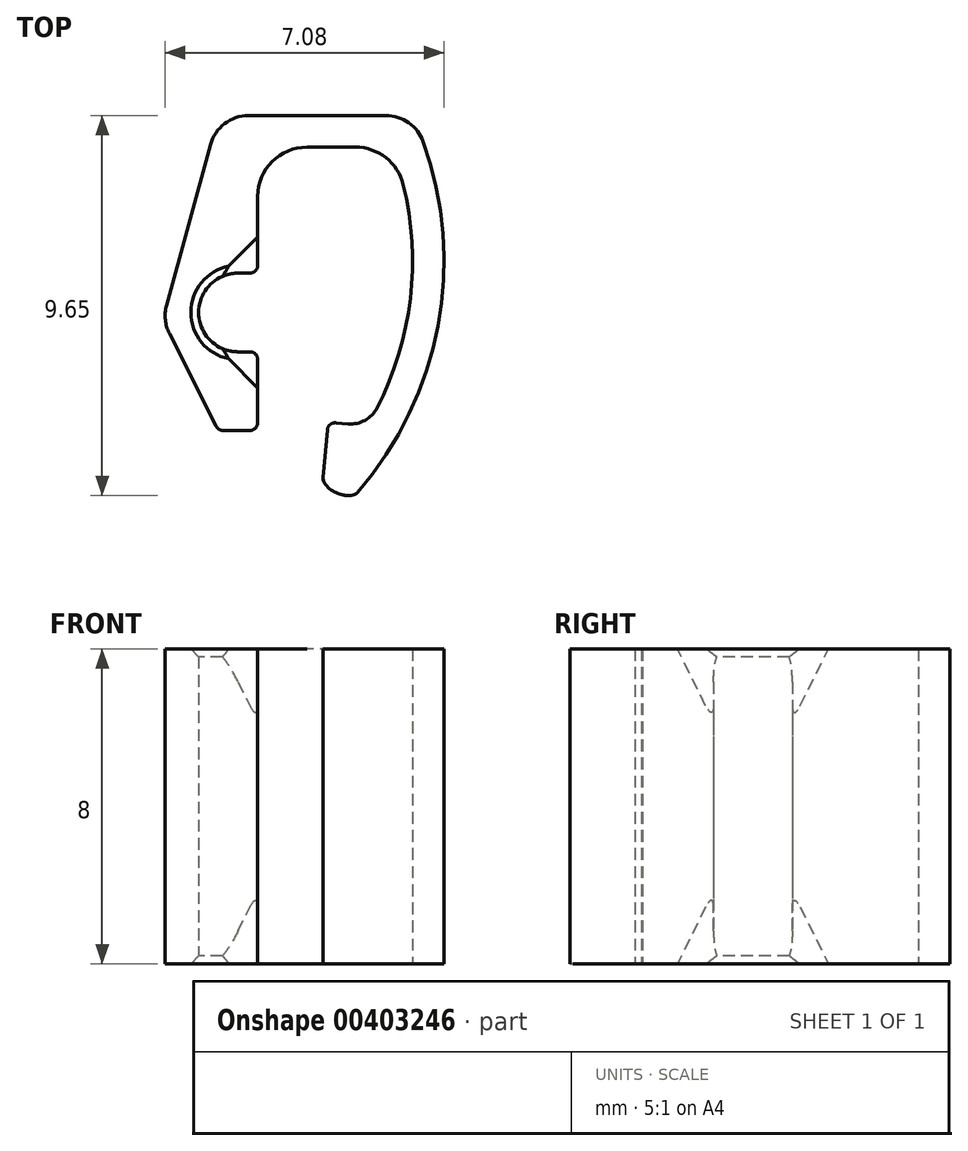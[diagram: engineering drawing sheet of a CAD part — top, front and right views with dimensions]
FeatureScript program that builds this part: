
annotation { "Feature Type Name" : "Feature", "Feature Type Description" : "" }
export const myFeature = defineFeature(function(context is Context, id is Id, definition is map)
    precondition{}
    {
        {
            var Q0;
            Q0=qCreatedBy(makeId("Top.planeOp"),FACE);
            var sketch = newSketch(context, id + "F0", { "sketchPlane" : qUnion([Q0])});
            skLineSegment(sketch, "E0", {"start": v(0, 0) * mm, "end": v(-0.62, -7.07) * mm, "construction": true});
            skLineSegment(sketch, "E1", {"start": v(-0.62, -7.07) * mm, "end": v(-1.62, -6.99) * mm});
            skLineSegment(sketch, "E2", {"start": v(-1.62, -6.99) * mm, "end": v(-1.86, -9.75) * mm});
            skLineSegment(sketch, "E3", {"start": v(0.53, 0.8) * mm, "end": v(-4.4, 0.8) * mm});
            skLineSegment(sketch, "E4", {"start": v(-3.9, -5.2) * mm, "end": v(-3.4, -5.2) * mm});
            skLineSegment(sketch, "E5", {"start": v(-3.4, -5.2) * mm, "end": v(-3.4, -7.2) * mm});
            skLineSegment(sketch, "E6", {"start": v(-5.82, -4.4) * mm, "end": v(-4.4, -7.2) * mm});
            skLineSegment(sketch, "E7", {"start": v(-4.4, -7.2) * mm, "end": v(-3.4, -7.2) * mm});
            skLineSegment(sketch, "E8", {"start": v(-3.4, -3.2) * mm, "end": v(-3.9, -3.2) * mm});
            skLineSegment(sketch, "E9", {"start": v(0, 0) * mm, "end": v(-3.4, 0) * mm});
            skLineSegment(sketch, "E10", {"start": v(-3.4, 0) * mm, "end": v(-3.4, -3.2) * mm});
            skArc(sketch, "E11", {"start": v(-3.9, -3.2) * mm, "mid": v(-4.9, -4.2) * mm, "end": v(-3.9, -5.2) * mm});
            skLineSegment(sketch, "E12", {"start": v(-5.82, -4.4) * mm, "end": v(-4.4, 0.8) * mm});
            skLineSegment(sketch, "E13", {"start": v(-4.4, -7.2) * mm, "end": v(-4.4, 0.8) * mm, "construction": true});
            skLineSegment(sketch, "E14", {"start": v(-3.9, -4.2) * mm, "end": v(-4.86, -3.94) * mm, "construction": true});
            skLineSegment(sketch, "E15", {"start": v(-4.86, -3.94) * mm, "end": v(-5.64, -3.73) * mm, "construction": true});
            skLineSegment(sketch, "E16", {"start": v(0, 0) * mm, "end": v(0, 0.8) * mm, "construction": true});
            skArc(sketch, "E17", {"start": v(-0.62, -7.07) * mm, "mid": v(0.5, -3.6) * mm, "end": v(0, 0) * mm});
            skArc(sketch, "E18", {"start": v(-1.86, -9.75) * mm, "mid": v(1.11, -4.88) * mm, "end": v(0.53, 0.8) * mm});
            skLineSegment(sketch, "E19", {"start": v(0.18, -7.3) * mm, "end": v(0.82, 0.08) * mm, "construction": true});
            skLineSegment(sketch, "E20", {"start": v(-3.4, -3.2) * mm, "end": v(-3.4, 0.8) * mm, "construction": true});
            skLineSegment(sketch, "E21", {"start": v(-3.9, -4.2) * mm, "end": v(-4.8, -4.65) * mm, "construction": true});
            skLineSegment(sketch, "E22", {"start": v(-4.8, -4.65) * mm, "end": v(-5.5, -5.01) * mm, "construction": true});
            skSolve(sketch);
        }
        {
            var Q0;
            Q0=qSketchRegion(id+"F0",true);
            extrude(context, id + "F1", {"entities" : qUnion([Q0]), "depth" : 4 * mm});
        }
        {
            var Q0;
            Q0=makeQuery(id+"F1.opExtrude","CAP_FACE",FACE,{"disambiguationData":[OSD([sQuery(id+"F0.wireOp",EDGE,"E0"),sQuery(id+"F0.wireOp",EDGE,"E1"),sQuery(id+"F0.wireOp",EDGE,"E2"),sQuery(id+"F0.wireOp",EDGE,"IWGYEIPr-8G1p-g9Af-FLij-pJIiTZfkYKLn"),sQuery(id+"F0.wireOp",EDGE,"bWUYzUkp-14V1-8Zip-sJGO-LbJPGX7ycxcC"),sQuery(id+"F0.wireOp",EDGE,"E3"),sQuery(id+"F0.wireOp",EDGE,"3qQk4eZ2-qFBK-7vCE-47k8-9gwiF50xY8QG"),sQuery(id+"F0.wireOp",EDGE,"FwfflrWr-MbD4-lGZ7-AJjG-6BkzjliF19me"),sQuery(id+"F0.wireOp",EDGE,"E4"),sQuery(id+"F0.wireOp",EDGE,"E5"),sQuery(id+"F0.wireOp",EDGE,"dEJFUDGW-VdPt-nXIw-TINV-OlQtnsbTHH9Y"),sQuery(id+"F0.wireOp",EDGE,"E6"),sQuery(id+"F0.wireOp",EDGE,"E7")])],"isStart":false});
            var sketch = newSketch(context, id + "F2", { "sketchPlane" : qUnion([Q0])});
            skLineSegment(sketch, "E23", {"start": v(-4.6, -4.9) * mm, "end": v(-3.4, -6.11) * mm});
            skLineSegment(sketch, "E24", {"start": v(-3.4, -6.11) * mm, "end": v(-3.4, -5.2) * mm});
            skLineSegment(sketch, "E25", {"start": v(-3.4, -5.2) * mm, "end": v(-4.6, -4.9) * mm});
            skLineSegment(sketch, "E26", {"start": v(-4.6, -3.5) * mm, "end": v(-3.4, -2.29) * mm});
            skLineSegment(sketch, "E27", {"start": v(-3.4, -2.29) * mm, "end": v(-3.4, -3.2) * mm});
            skLineSegment(sketch, "E28", {"start": v(-3.4, -3.2) * mm, "end": v(-4.6, -3.5) * mm});
            skSolve(sketch);
        }
        {
            var Q0;
            Q0=qSketchRegion(id+"F2",true);
            extrude(context, id + "F3", {"entities" : qUnion([Q0]), "operationType" : NewBodyOperationType.REMOVE, "oppositeDirection" : true, "depth" : 2 * mm});
        }
        {
            var Q0;
            Q0=makeQuery(id+"F3.boolean.opBoolean","COPY",EDGE,{"derivedFrom":makeQuery(id+"F3.opExtrude","CAP_EDGE",EDGE,{"disambiguationData":[OSD([sQuery(id+"F2.wireOp",EDGE,"E23")])],"isStart":false})});
            chamfer(context, id + "F4", {"entities" : qUnion([Q0]), "chamferType" : ChamferType.TWO_OFFSETS, "width1" : .7 * mm, "oppositeDirection" : false, "width2" : 2 * mm, "tangentPropagation" : true});
        }
        {
            var Q0;
            Q0=makeQuery(id+"F3.boolean.opBoolean","COPY",EDGE,{"derivedFrom":makeQuery(id+"F3.opExtrude","CAP_EDGE",EDGE,{"disambiguationData":[OSD([sQuery(id+"F2.wireOp",EDGE,"E26")])],"isStart":false})});
            chamfer(context, id + "F5", {"entities" : qUnion([Q0]), "chamferType" : ChamferType.TWO_OFFSETS, "width1" : 2 * mm, "oppositeDirection" : false, "width2" : .7 * mm, "tangentPropagation" : true});
        }
        {
            var Q0;
            Q0=makeQuery(id+"F1.opExtrude","SWEPT_EDGE",EDGE,{"disambiguationData":[OSD([sQuery(id+"F0.wireOp",EDGE,"E1"),sQuery(id+"F0.wireOp",EDGE,"E2")])]});
            var Q1;
            Q1=makeQuery(id+"F1.opExtrude","SWEPT_EDGE",EDGE,{"disambiguationData":[OSD([sQuery(id+"F0.wireOp",EDGE,"E5"),sQuery(id+"F0.wireOp",EDGE,"E7")])]});
            var Q2;
            Q2=makeQuery(id+"F1.opExtrude","SWEPT_EDGE",EDGE,{"disambiguationData":[OSD([sQuery(id+"F0.wireOp",EDGE,"E4"),sQuery(id+"F0.wireOp",EDGE,"E5")])]});
            var Q3;
            Q3=makeQuery(id+"F1.opExtrude","SWEPT_EDGE",EDGE,{"disambiguationData":[OSD([sQuery(id+"F0.wireOp",EDGE,"E8"),sQuery(id+"F0.wireOp",EDGE,"E10")])]});
            var Q4;
            Q4=makeQuery(id+"F1.opExtrude","SWEPT_EDGE",EDGE,{"disambiguationData":[OSD([sQuery(id+"F0.wireOp",EDGE,"E6"),sQuery(id+"F0.wireOp",EDGE,"E7")])]});
            fillet(context, id + "F6", {"entities" : qUnion([Q0, Q1, Q2, Q3, Q4]), "radius" : .2 * mm, "tangentPropagation" : true, "allowEdgeOverflow" : false});
        }
        {
            var Q0;
            Q0=makeQuery(id+"F1.opExtrude","SWEPT_EDGE",EDGE,{"disambiguationData":[OSD([sQuery(id+"F0.wireOp",EDGE,"bWUYzUkp-14V1-8Zip-sJGO-LbJPGX7ycxcC"),sQuery(id+"F0.wireOp",EDGE,"E3")])]});
            var Q1;
            Q1=makeQuery(id+"F1.opExtrude","SWEPT_EDGE",EDGE,{"disambiguationData":[OSD([sQuery(id+"F0.wireOp",EDGE,"IWGYEIPr-8G1p-g9Af-FLij-pJIiTZfkYKLn"),sQuery(id+"F0.wireOp",EDGE,"bWUYzUkp-14V1-8Zip-sJGO-LbJPGX7ycxcC")])]});
            var Q2;
            Q2=makeQuery(id+"F1.opExtrude","SWEPT_EDGE",EDGE,{"disambiguationData":[OSD([sQuery(id+"F0.wireOp",EDGE,"E6"),sQuery(id+"F0.wireOp",EDGE,"E7")])]});
            var Q3;
            Q3=makeQuery(id+"F1.opExtrude","SWEPT_EDGE",EDGE,{"disambiguationData":[OSD([sQuery(id+"F0.wireOp",EDGE,"E6"),sQuery(id+"F0.wireOp",EDGE,"E12")])]});
            var Q4;
            Q4=makeQuery(id+"F1.opExtrude","SWEPT_EDGE",EDGE,{"disambiguationData":[OSD([sQuery(id+"F0.wireOp",EDGE,"E3"),sQuery(id+"F0.wireOp",EDGE,"E12")])]});
            fillet(context, id + "F7", {"entities" : qUnion([Q0, Q1, Q2, Q3, Q4]), "radius" : 1 * mm, "tangentPropagation" : true, "allowEdgeOverflow" : false});
        }
        {
            var Q0;
            Q0=makeQuery(id+"F1.opExtrude","SWEPT_EDGE",EDGE,{"disambiguationData":[OSD([sQuery(id+"F0.wireOp",EDGE,"E9"),sQuery(id+"F0.wireOp",EDGE,"E10")])]});
            var Q1;
            Q1=makeQuery(id+"F1.opExtrude","SWEPT_EDGE",EDGE,{"disambiguationData":[OSD([sQuery(id+"F0.wireOp",EDGE,"E9"),sQuery(id+"F0.wireOp",EDGE,"E17")])]});
            fillet(context, id + "F8", {"entities" : qUnion([Q0, Q1]), "radius" : 1.25 * mm, "tangentPropagation" : true, "allowEdgeOverflow" : false});
        }
        {
            var Q0;
            Q0=makeQuery(id+"F1.opExtrude","CAP_EDGE",EDGE,{"disambiguationData":[OSD([sQuery(id+"F0.wireOp",EDGE,"E11")])],"isStart":false});
            chamfer(context, id + "F9", {"entities" : qUnion([Q0]), "chamferType" : ChamferType.OFFSET_ANGLE, "width" : .2 * mm, "oppositeDirection" : false, "angle" : 45 * degree, "tangentPropagation" : true});
        }
        {
            var Q0;
            Q0=makeQuery(id+"F1.opExtrude","SWEPT_BODY",BODY,{"disambiguationData":[OSD([sQuery(id+"F0.wireOp",EDGE,"E0"),sQuery(id+"F0.wireOp",EDGE,"E1"),sQuery(id+"F0.wireOp",EDGE,"E2"),sQuery(id+"F0.wireOp",EDGE,"IWGYEIPr-8G1p-g9Af-FLij-pJIiTZfkYKLn"),sQuery(id+"F0.wireOp",EDGE,"bWUYzUkp-14V1-8Zip-sJGO-LbJPGX7ycxcC"),sQuery(id+"F0.wireOp",EDGE,"E3"),sQuery(id+"F0.wireOp",EDGE,"3qQk4eZ2-qFBK-7vCE-47k8-9gwiF50xY8QG"),sQuery(id+"F0.wireOp",EDGE,"FwfflrWr-MbD4-lGZ7-AJjG-6BkzjliF19me"),sQuery(id+"F0.wireOp",EDGE,"E4"),sQuery(id+"F0.wireOp",EDGE,"E5"),sQuery(id+"F0.wireOp",EDGE,"dEJFUDGW-VdPt-nXIw-TINV-OlQtnsbTHH9Y"),sQuery(id+"F0.wireOp",EDGE,"E6"),sQuery(id+"F0.wireOp",EDGE,"E7")])]});
            var Q1;
            Q1=makeQuery(id+"F1.opExtrude","CAP_FACE",FACE,{"disambiguationData":[OSD([sQuery(id+"F0.wireOp",EDGE,"E0"),sQuery(id+"F0.wireOp",EDGE,"E1"),sQuery(id+"F0.wireOp",EDGE,"E2"),sQuery(id+"F0.wireOp",EDGE,"IWGYEIPr-8G1p-g9Af-FLij-pJIiTZfkYKLn"),sQuery(id+"F0.wireOp",EDGE,"bWUYzUkp-14V1-8Zip-sJGO-LbJPGX7ycxcC"),sQuery(id+"F0.wireOp",EDGE,"E3"),sQuery(id+"F0.wireOp",EDGE,"3qQk4eZ2-qFBK-7vCE-47k8-9gwiF50xY8QG"),sQuery(id+"F0.wireOp",EDGE,"FwfflrWr-MbD4-lGZ7-AJjG-6BkzjliF19me"),sQuery(id+"F0.wireOp",EDGE,"E4"),sQuery(id+"F0.wireOp",EDGE,"E5"),sQuery(id+"F0.wireOp",EDGE,"dEJFUDGW-VdPt-nXIw-TINV-OlQtnsbTHH9Y"),sQuery(id+"F0.wireOp",EDGE,"E6"),sQuery(id+"F0.wireOp",EDGE,"E7")])],"isStart":true});
            mirror(context, id + "F10", {"operationType" : NewBodyOperationType.ADD, "entities" : qUnion([Q0]), "mirrorPlane" : qUnion([Q1])});
        }
        {
            var Q0;
            {var subQ0=makeQuery(id+"F1.opExtrude","SWEPT_EDGE",EDGE,{"disambiguationData":[OSD([sQuery(id+"F0.wireOp",EDGE,"E1"),sQuery(id+"F0.wireOp",EDGE,"E17")])]});Q0=makeQuery(id+"F10.boolean.opBoolean","MERGE",EDGE,{"derivedFrom":[subQ0,makeQuery(id+"F10.opPattern","COPY",EDGE,{"derivedFrom":subQ0,"instanceName":"1"})]});}
            fillet(context, id + "F11", {"entities" : qUnion([Q0]), "radius" : .75 * mm, "tangentPropagation" : true, "allowEdgeOverflow" : false});
        }
        {
            var Q0;
            {var subQ0=makeQuery(id+"F1.opExtrude","SWEPT_EDGE",EDGE,{"disambiguationData":[OSD([sQuery(id+"F0.wireOp",EDGE,"E2"),sQuery(id+"F0.wireOp",EDGE,"E18")])]});Q0=makeQuery(id+"F10.boolean.opBoolean","MERGE",EDGE,{"derivedFrom":[subQ0,makeQuery(id+"F10.opPattern","COPY",EDGE,{"derivedFrom":subQ0,"instanceName":"1"})]});}
            fillet(context, id + "F12", {"entities" : qUnion([Q0]), "radius" : .5 * mm, "tangentPropagation" : true, "rho" : .15, "crossSection" : FilletCrossSection.CONIC, "allowEdgeOverflow" : false});
        }
    });
